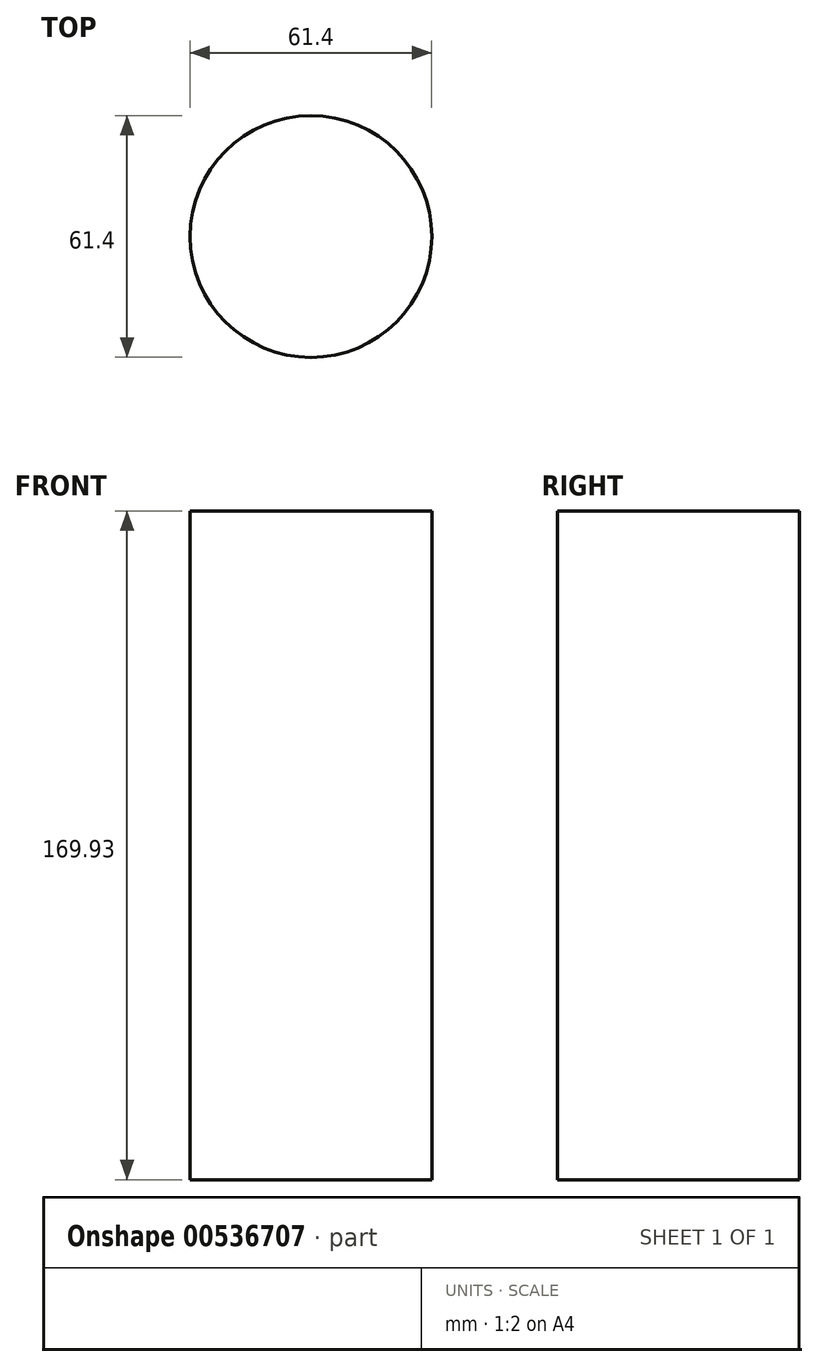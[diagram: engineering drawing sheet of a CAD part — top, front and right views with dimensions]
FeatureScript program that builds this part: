
annotation { "Feature Type Name" : "Feature", "Feature Type Description" : "" }
export const myFeature = defineFeature(function(context is Context, id is Id, definition is map)
    precondition{}
    {
        {
            var Q0;
            Q0=qCreatedBy(makeId("Top.planeOp"),FACE);
            var sketch = newSketch(context, id + "F0", { "sketchPlane" : qUnion([Q0])});
            skCircle(sketch, "E0", {"center": v(0, 0) * mm, "radius": 30.7 * mm});
            skSolve(sketch);
        }
        {
            var Q0;
            Q0 = qSketchRegion(id + "F0", true);
            extrude(context, id + "F1", {"entities" : qUnion([Q0]), "depth" : 169.93 * mm, "offsetDistance" : 25.4 * mm});
        }
        {
            var Q0;
            Q0=makeQuery(id+"F1.opExtrude","CAP_FACE",FACE,{"disambiguationData":[OSD([sQuery(id+"F0.wireOp",EDGE,"E0")])],"isStart":true});
            extrude(context, id + "F2", {"entities" : qUnion([Q0]), "operationType" : NewBodyOperationType.ADD, "oppositeDirection" : true, "depth" : 165.35 * mm, "offsetDistance" : 25.4 * mm});
        }
    });
